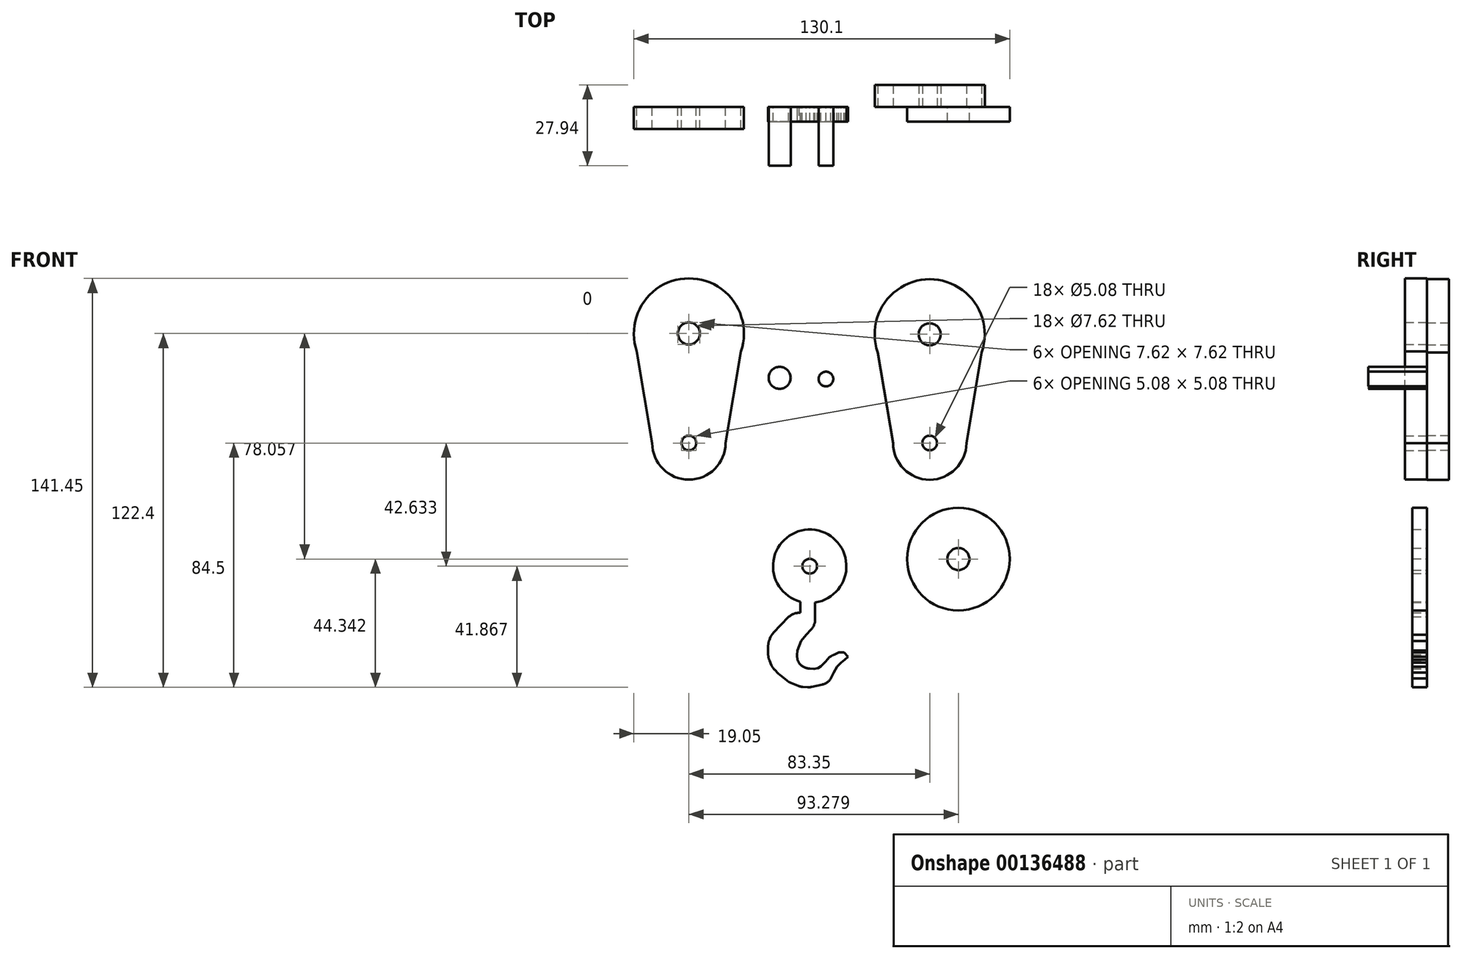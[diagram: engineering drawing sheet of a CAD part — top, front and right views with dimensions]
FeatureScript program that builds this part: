
annotation { "Feature Type Name" : "Feature", "Feature Type Description" : "" }
export const myFeature = defineFeature(function(context is Context, id is Id, definition is map)
    precondition{}
    {
        {
            var Q0;
            Q0=qCreatedBy(makeId("Front.planeOp"),FACE);
            var sketch = newSketch(context, id + "F0", { "sketchPlane" : qUnion([Q0])});
            skCircle(sketch, "E0", {"center": v(-41.82, 37.9) * mm, "radius": 19.05 * mm});
            skCircle(sketch, "E1", {"center": v(-41.82, 0) * mm, "radius": 12.69 * mm});
            skLineSegment(sketch, "E2", {"start": v(-54.5, 0) * mm, "end": v(-60.87, 37.9) * mm});
            skLineSegment(sketch, "E3", {"start": v(-29.13, 0) * mm, "end": v(-22.77, 37.9) * mm});
            skSolve(sketch);
        }
        {
            var Q0;
            Q0 = qSketchRegion(id + "F0", true);
            extrude(context, id + "F1", {"entities" : qUnion([Q0]), "depth" : 7.62 * mm});
        }
        {
            var Q0;
            Q0=sQuery(id+"F0.wireOp",VERTEX,"E1.center");
            var Q1;
            Q1=makeQuery(id+"F1.opExtrude","SWEPT_BODY",BODY,{"disambiguationData":[OSD([sQuery(id+"F0.wireOp",EDGE,"E0"),sQuery(id+"F0.wireOp",EDGE,"E1"),sQuery(id+"F0.wireOp",EDGE,"E2"),sQuery(id+"F0.wireOp",EDGE,"E3")])]});
            hole(context, id + "F2", {"style" : HoleStyle.SIMPLE, "endStyle" : HoleEndStyle.THROUGH, "oppositeDirection" : true, "holeDiameter" : 5.08 * mm, "locations" : qUnion([Q0]), "scope" : qUnion([Q1]), "isTappedThrough" : true});
        }
        {
            var Q0;
            Q0=qCreatedBy(makeId("Front.planeOp"),FACE);
            var sketch = newSketch(context, id + "F3", { "sketchPlane" : qUnion([Q0])});
            skCircle(sketch, "E4", {"center": v(41.53, 37.6) * mm, "radius": 19.06 * mm});
            skCircle(sketch, "E5", {"center": v(41.53, 0) * mm, "radius": 12.7 * mm});
            skLineSegment(sketch, "E6", {"start": v(54.23, 0) * mm, "end": v(60.59, 37.6) * mm});
            skLineSegment(sketch, "E7", {"start": v(28.83, 0) * mm, "end": v(22.47, 37.6) * mm});
            skSolve(sketch);
        }
        {
            var Q0;
            Q0 = qSketchRegion(id + "F3", true);
            extrude(context, id + "F4", {"entities" : qUnion([Q0]), "oppositeDirection" : true, "depth" : 7.62 * mm});
        }
        {
            var Q0;
            Q0=sQuery(id+"F0.wireOp",VERTEX,"E0.center");
            var Q1;
            Q1=makeQuery(id+"F1.opExtrude","SWEPT_BODY",BODY,{"disambiguationData":[OSD([sQuery(id+"F0.wireOp",EDGE,"E0"),sQuery(id+"F0.wireOp",EDGE,"E1"),sQuery(id+"F0.wireOp",EDGE,"E2"),sQuery(id+"F0.wireOp",EDGE,"E3")])]});
            hole(context, id + "F5", {"style" : HoleStyle.SIMPLE, "endStyle" : HoleEndStyle.THROUGH, "oppositeDirection" : true, "holeDiameter" : 7.62 * mm, "locations" : qUnion([Q0]), "scope" : qUnion([Q1]), "isTappedThrough" : true});
        }
        {
            var Q0;
            Q0=sQuery(id+"F3.wireOp",VERTEX,"E4.center");
            var Q1;
            Q1=makeQuery(id+"F4.opExtrude","SWEPT_BODY",BODY,{"disambiguationData":[OSD([sQuery(id+"F3.wireOp",EDGE,"E4"),sQuery(id+"F3.wireOp",EDGE,"E5"),sQuery(id+"F3.wireOp",EDGE,"E6"),sQuery(id+"F3.wireOp",EDGE,"E7")])]});
            hole(context, id + "F6", {"style" : HoleStyle.SIMPLE, "endStyle" : HoleEndStyle.THROUGH, "holeDiameter" : 7.62 * mm, "locations" : qUnion([Q0]), "scope" : qUnion([Q1]), "isTappedThrough" : true});
        }
        {
            var Q0;
            Q0=sQuery(id+"F3.wireOp",VERTEX,"E5.center");
            var Q1;
            Q1=makeQuery(id+"F4.opExtrude","SWEPT_BODY",BODY,{"disambiguationData":[OSD([sQuery(id+"F3.wireOp",EDGE,"E4"),sQuery(id+"F3.wireOp",EDGE,"E5"),sQuery(id+"F3.wireOp",EDGE,"E6"),sQuery(id+"F3.wireOp",EDGE,"E7")])]});
            hole(context, id + "F7", {"style" : HoleStyle.SIMPLE, "endStyle" : HoleEndStyle.THROUGH, "holeDiameter" : 5.08 * mm, "locations" : qUnion([Q0]), "scope" : qUnion([Q1]), "isTappedThrough" : true});
        }
        {
            var Q0;
            Q0=qCreatedBy(makeId("Front.planeOp"),FACE);
            var sketch = newSketch(context, id + "F8", { "sketchPlane" : qUnion([Q0])});
            skCircle(sketch, "E8", {"center": v(0, -42.63) * mm, "radius": 12.7 * mm});
            skLineSegment(sketch, "E9", {"start": v(-3.22, -54.92) * mm, "end": v(-3.22, -58.76) * mm});
            skLineSegment(sketch, "E10", {"start": v(-3.22, -58.76) * mm, "end": v(-5.48, -58.76) * mm});
            skLineSegment(sketch, "E11", {"start": v(-5.48, -58.76) * mm, "end": v(-7.3, -60.18) * mm});
            skLineSegment(sketch, "E12", {"start": v(-7.3, -60.18) * mm, "end": v(-13.26, -66.45) * mm});
            skLineSegment(sketch, "E13", {"start": v(-13.26, -66.45) * mm, "end": v(-14.37, -69.07) * mm});
            skLineSegment(sketch, "E14", {"start": v(-14.37, -69.07) * mm, "end": v(-14.37, -71.6) * mm});
            skLineSegment(sketch, "E15", {"start": v(-14.37, -71.6) * mm, "end": v(-14.37, -74.23) * mm});
            skLineSegment(sketch, "E16", {"start": v(-14.37, -74.23) * mm, "end": v(-12.85, -77.76) * mm});
            skLineSegment(sketch, "E17", {"start": v(-12.85, -77.76) * mm, "end": v(-10.63, -79.99) * mm});
            skLineSegment(sketch, "E18", {"start": v(-10.63, -79.99) * mm, "end": v(-7.2, -82.72) * mm});
            skLineSegment(sketch, "E19", {"start": v(-7.2, -82.72) * mm, "end": v(-3.25, -84.33) * mm});
            skLineSegment(sketch, "E20", {"start": v(-3.25, -84.33) * mm, "end": v(0, -84.53) * mm});
            skLineSegment(sketch, "E21", {"start": v(0, -84.53) * mm, "end": v(6.35, -83.12) * mm});
            skLineSegment(sketch, "E22", {"start": v(1.88, -55.2) * mm, "end": v(1.88, -59.17) * mm});
            skLineSegment(sketch, "E23", {"start": v(1.88, -59.17) * mm, "end": v(1.88, -61.4) * mm});
            skLineSegment(sketch, "E24", {"start": v(1.88, -61.4) * mm, "end": v(1.88, -62.9) * mm});
            skLineSegment(sketch, "E25", {"start": v(1.88, -62.9) * mm, "end": v(0.9, -64.12) * mm});
            skLineSegment(sketch, "E26", {"start": v(-4.47, -75.04) * mm, "end": v(-2.65, -77.76) * mm});
            skLineSegment(sketch, "E27", {"start": v(-2.65, -77.76) * mm, "end": v(0, -78.07) * mm});
            skLineSegment(sketch, "E28", {"start": v(0, -78.07) * mm, "end": v(1.5, -78.17) * mm});
            skLineSegment(sketch, "E29", {"start": v(1.5, -78.17) * mm, "end": v(2.91, -77.97) * mm});
            skLineSegment(sketch, "E30", {"start": v(2.91, -77.97) * mm, "end": v(3.82, -77.26) * mm});
            skLineSegment(sketch, "E31", {"start": v(3.82, -77.26) * mm, "end": v(5.64, -75.44) * mm});
            skLineSegment(sketch, "E32", {"start": v(5.64, -75.44) * mm, "end": v(6.95, -73.72) * mm});
            skLineSegment(sketch, "E33", {"start": v(6.95, -73.72) * mm, "end": v(8.57, -73.22) * mm});
            skLineSegment(sketch, "E34", {"start": v(8.57, -73.22) * mm, "end": v(10.09, -72.5) * mm});
            skLineSegment(sketch, "E35", {"start": v(10.09, -72.5) * mm, "end": v(11.9, -72.5) * mm});
            skLineSegment(sketch, "E36", {"start": v(11.9, -72.5) * mm, "end": v(13.22, -73.92) * mm});
            skLineSegment(sketch, "E37", {"start": v(13.22, -73.92) * mm, "end": v(12.07, -75) * mm});
            skLineSegment(sketch, "E38", {"start": v(12.07, -75) * mm, "end": v(10.8, -76.05) * mm});
            skLineSegment(sketch, "E39", {"start": v(10.8, -76.05) * mm, "end": v(9.48, -77.46) * mm});
            skLineSegment(sketch, "E40", {"start": v(9.48, -77.46) * mm, "end": v(8.27, -79.48) * mm});
            skLineSegment(sketch, "E41", {"start": v(8.27, -79.48) * mm, "end": v(7.36, -81.5) * mm});
            skLineSegment(sketch, "E42", {"start": v(7.36, -81.5) * mm, "end": v(6.35, -83.12) * mm});
            skPoint(sketch, "E43.startSnap0", {"position": v(1.39, -63.51) * mm});
            skLineSegment(sketch, "E44", {"start": v(0.9, -64.12) * mm, "end": v(-1.23, -66.34) * mm});
            skLineSegment(sketch, "E45", {"start": v(-1.23, -66.34) * mm, "end": v(-2.95, -68.57) * mm});
            skLineSegment(sketch, "E46", {"start": v(-2.95, -68.57) * mm, "end": v(-4.26, -71.8) * mm});
            skLineSegment(sketch, "E47", {"start": v(-4.26, -71.8) * mm, "end": v(-4.47, -75.04) * mm});
            skSolve(sketch);
        }
        {
            var Q0;
            Q0 = qSketchRegion(id + "F8", true);
            extrude(context, id + "F9", {"entities" : qUnion([Q0]), "depth" : 5.08 * mm});
        }
        {
            var Q0;
            Q0=makeQuery(id+"F9.opExtrude","SWEPT_EDGE",EDGE,{"disambiguationData":[OSD([sQuery(id+"F8.wireOp",EDGE,"E21"),sQuery(id+"F8.wireOp",EDGE,"E42")])]});
            fillet(context, id + "F10", {"entities" : qUnion([Q0]), "radius" : 5.08 * mm, "tangentPropagation" : true, "allowEdgeOverflow" : false});
        }
        {
            var Q0;
            Q0=makeQuery(id+"F9.opExtrude","SWEPT_EDGE",EDGE,{"disambiguationData":[OSD([sQuery(id+"F8.wireOp",EDGE,"E19"),sQuery(id+"F8.wireOp",EDGE,"E20")])]});
            var Q1;
            Q1=makeQuery(id+"F9.opExtrude","SWEPT_EDGE",EDGE,{"disambiguationData":[OSD([sQuery(id+"F8.wireOp",EDGE,"E18"),sQuery(id+"F8.wireOp",EDGE,"E19")])]});
            var Q2;
            Q2=makeQuery(id+"F9.opExtrude","SWEPT_EDGE",EDGE,{"disambiguationData":[OSD([sQuery(id+"F8.wireOp",EDGE,"E17"),sQuery(id+"F8.wireOp",EDGE,"E18")])]});
            var Q3;
            Q3=makeQuery(id+"F9.opExtrude","SWEPT_EDGE",EDGE,{"disambiguationData":[OSD([sQuery(id+"F8.wireOp",EDGE,"E20"),sQuery(id+"F8.wireOp",EDGE,"E21")])]});
            fillet(context, id + "F11", {"entities" : qUnion([Q0, Q1, Q2, Q3]), "radius" : 5.08 * mm, "tangentPropagation" : true, "allowEdgeOverflow" : false});
        }
        {
            var Q0;
            Q0=makeQuery(id+"F9.opExtrude","SWEPT_EDGE",EDGE,{"disambiguationData":[OSD([sQuery(id+"F8.wireOp",EDGE,"E32"),sQuery(id+"F8.wireOp",EDGE,"E33")])]});
            fillet(context, id + "F12", {"entities" : qUnion([Q0]), "radius" : 5.08 * mm, "tangentPropagation" : true, "allowEdgeOverflow" : false});
        }
        {
            var Q0;
            Q0=makeQuery(id+"F9.opExtrude","SWEPT_EDGE",EDGE,{"disambiguationData":[OSD([sQuery(id+"F8.wireOp",EDGE,"E15"),sQuery(id+"F8.wireOp",EDGE,"E16")])]});
            var Q1;
            Q1=makeQuery(id+"F9.opExtrude","SWEPT_EDGE",EDGE,{"disambiguationData":[OSD([sQuery(id+"F8.wireOp",EDGE,"E10"),sQuery(id+"F8.wireOp",EDGE,"E11")])]});
            fillet(context, id + "F13", {"entities" : qUnion([Q0, Q1]), "radius" : 5.08 * mm, "tangentPropagation" : true, "allowEdgeOverflow" : false});
        }
        {
            var Q0;
            Q0=makeQuery(id+"F9.opExtrude","SWEPT_EDGE",EDGE,{"disambiguationData":[OSD([sQuery(id+"F8.wireOp",EDGE,"E26"),sQuery(id+"F8.wireOp",EDGE,"E47")])]});
            var Q1;
            Q1=makeQuery(id+"F9.opExtrude","SWEPT_EDGE",EDGE,{"disambiguationData":[OSD([sQuery(id+"F8.wireOp",EDGE,"E26"),sQuery(id+"F8.wireOp",EDGE,"E27")])]});
            var Q2;
            Q2=makeQuery(id+"F9.opExtrude","SWEPT_EDGE",EDGE,{"disambiguationData":[OSD([sQuery(id+"F8.wireOp",EDGE,"E24"),sQuery(id+"F8.wireOp",EDGE,"E25")])]});
            fillet(context, id + "F14", {"entities" : qUnion([Q0, Q1, Q2]), "radius" : 5.08 * mm, "tangentPropagation" : true, "allowEdgeOverflow" : false});
        }
        {
            var Q0;
            Q0=makeQuery(id+"F9.opExtrude","SWEPT_EDGE",EDGE,{"disambiguationData":[OSD([sQuery(id+"F8.wireOp",EDGE,"E12"),sQuery(id+"F8.wireOp",EDGE,"E13")])]});
            var Q1;
            Q1=makeQuery(id+"F9.opExtrude","SWEPT_EDGE",EDGE,{"disambiguationData":[OSD([sQuery(id+"F8.wireOp",EDGE,"E13"),sQuery(id+"F8.wireOp",EDGE,"E14")])]});
            var Q2;
            Q2=makeQuery(id+"F9.opExtrude","SWEPT_EDGE",EDGE,{"disambiguationData":[OSD([sQuery(id+"F8.wireOp",EDGE,"E16"),sQuery(id+"F8.wireOp",EDGE,"E17")])]});
            fillet(context, id + "F15", {"entities" : qUnion([Q0, Q1, Q2]), "radius" : 5.08 * mm, "tangentPropagation" : true, "allowEdgeOverflow" : false});
        }
        {
            var Q0;
            Q0=sQuery(id+"F8.wireOp",VERTEX,"E8.center");
            var Q1;
            Q1=makeQuery(id+"F9.opExtrude","SWEPT_BODY",BODY,{"disambiguationData":[OSD([sQuery(id+"F8.wireOp",EDGE,"E8"),sQuery(id+"F8.wireOp",EDGE,"E9"),sQuery(id+"F8.wireOp",EDGE,"E10"),sQuery(id+"F8.wireOp",EDGE,"E11"),sQuery(id+"F8.wireOp",EDGE,"E12"),sQuery(id+"F8.wireOp",EDGE,"E13"),sQuery(id+"F8.wireOp",EDGE,"E14"),sQuery(id+"F8.wireOp",EDGE,"E15"),sQuery(id+"F8.wireOp",EDGE,"E16"),sQuery(id+"F8.wireOp",EDGE,"E17"),sQuery(id+"F8.wireOp",EDGE,"E18"),sQuery(id+"F8.wireOp",EDGE,"E19"),sQuery(id+"F8.wireOp",EDGE,"E20"),sQuery(id+"F8.wireOp",EDGE,"E21"),sQuery(id+"F8.wireOp",EDGE,"E22"),sQuery(id+"F8.wireOp",EDGE,"E23"),sQuery(id+"F8.wireOp",EDGE,"E24"),sQuery(id+"F8.wireOp",EDGE,"E25"),sQuery(id+"F8.wireOp",EDGE,"E26"),sQuery(id+"F8.wireOp",EDGE,"E27"),sQuery(id+"F8.wireOp",EDGE,"E28"),sQuery(id+"F8.wireOp",EDGE,"E29"),sQuery(id+"F8.wireOp",EDGE,"E30"),sQuery(id+"F8.wireOp",EDGE,"E31"),sQuery(id+"F8.wireOp",EDGE,"E32"),sQuery(id+"F8.wireOp",EDGE,"E33"),sQuery(id+"F8.wireOp",EDGE,"E34"),sQuery(id+"F8.wireOp",EDGE,"E35"),sQuery(id+"F8.wireOp",EDGE,"E36"),sQuery(id+"F8.wireOp",EDGE,"E37"),sQuery(id+"F8.wireOp",EDGE,"E38"),sQuery(id+"F8.wireOp",EDGE,"E39"),sQuery(id+"F8.wireOp",EDGE,"E40"),sQuery(id+"F8.wireOp",EDGE,"E41"),sQuery(id+"F8.wireOp",EDGE,"E42"),sQuery(id+"F8.wireOp",EDGE,"E44"),sQuery(id+"F8.wireOp",EDGE,"E45"),sQuery(id+"F8.wireOp",EDGE,"E46"),sQuery(id+"F8.wireOp",EDGE,"E47")])]});
            hole(context, id + "F16", {"style" : HoleStyle.SIMPLE, "endStyle" : HoleEndStyle.THROUGH, "oppositeDirection" : true, "holeDiameter" : 5.08 * mm, "locations" : qUnion([Q0]), "scope" : qUnion([Q1]), "isTappedThrough" : true});
        }
        {
            var Q0;
            Q0=qCreatedBy(makeId("Front.planeOp"),FACE);
            var sketch = newSketch(context, id + "F17", { "sketchPlane" : qUnion([Q0])});
            skCircle(sketch, "E48", {"center": v(51.46, -40.16) * mm, "radius": 17.77 * mm});
            skSolve(sketch);
        }
        {
            var Q0;
            Q0 = qSketchRegion(id + "F17", true);
            extrude(context, id + "F18", {"entities" : qUnion([Q0]), "depth" : 5.08 * mm});
        }
        {
            var Q0;
            Q0=sQuery(id+"F17.wireOp",VERTEX,"E48.center");
            var Q1;
            Q1=makeQuery(id+"F18.opExtrude","SWEPT_BODY",BODY,{"disambiguationData":[OSD([sQuery(id+"F17.wireOp",EDGE,"E48")])]});
            hole(context, id + "F19", {"style" : HoleStyle.SIMPLE, "endStyle" : HoleEndStyle.THROUGH, "oppositeDirection" : true, "holeDiameter" : 7.62 * mm, "locations" : qUnion([Q0]), "scope" : qUnion([Q1]), "isTappedThrough" : true});
        }
        {
            var Q0;
            Q0=qCreatedBy(makeId("Front.planeOp"),FACE);
            var sketch = newSketch(context, id + "F20", { "sketchPlane" : qUnion([Q0])});
            skCircle(sketch, "E49", {"center": v(-10.4, 22.55) * mm, "radius": 3.8 * mm});
            skCircle(sketch, "E50", {"center": v(5.63, 22.13) * mm, "radius": 2.55 * mm});
            skSolve(sketch);
        }
        {
            var Q0;
            Q0 = qSketchRegion(id + "F20", true);
            extrude(context, id + "F21", {"entities" : qUnion([Q0]), "depth" : 20.32 * mm});
        }
    });
